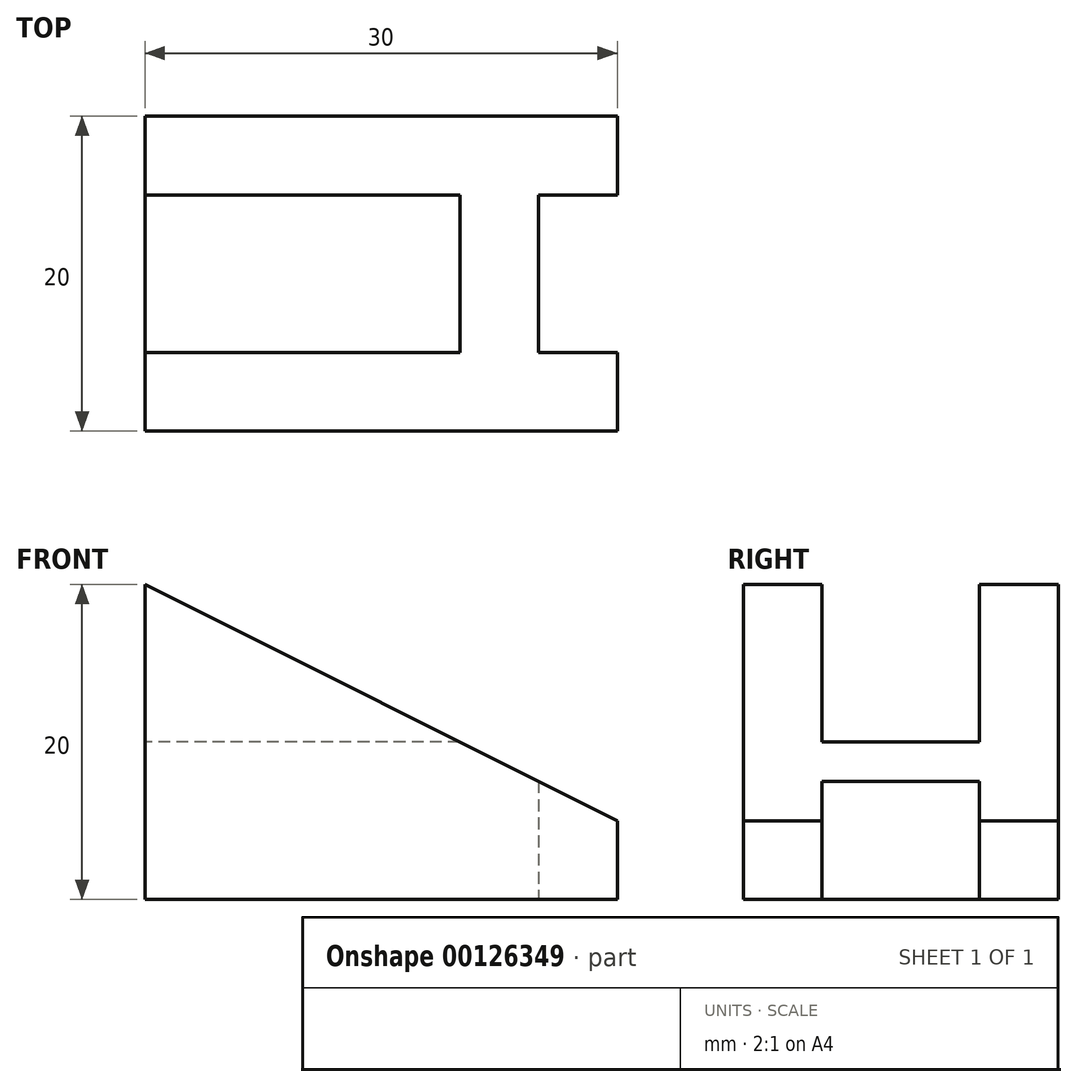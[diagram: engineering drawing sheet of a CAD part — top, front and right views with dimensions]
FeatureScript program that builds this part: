
annotation { "Feature Type Name" : "Feature", "Feature Type Description" : "" }
export const myFeature = defineFeature(function(context is Context, id is Id, definition is map)
    precondition{}
    {
        {
            var Q0;
            Q0=qCreatedBy(makeId("Front.planeOp"),FACE);
            var sketch = newSketch(context, id + "F0", { "sketchPlane" : qUnion([Q0])});
            skLineSegment(sketch, "E0", {"start": v(0, 0) * mm, "end": v(0, 20) * mm});
            skLineSegment(sketch, "E1", {"start": v(0, 20) * mm, "end": v(30, 5) * mm});
            skLineSegment(sketch, "E2", {"start": v(30, 5) * mm, "end": v(30, 0) * mm});
            skLineSegment(sketch, "E3", {"start": v(30, 0) * mm, "end": v(0, 0) * mm});
            skSolve(sketch);
        }
        {
            var Q0;
            Q0 = qSketchRegion(id + "F0", true);
            extrude(context, id + "F1", {"entities" : qUnion([Q0]), "endBound" : BoundingType.SYMMETRIC, "depth" : 20 * mm});
        }
        {
            var Q0;
            Q0=makeQuery(id+"F1.opExtrude","SWEPT_FACE",FACE,{"disambiguationData":[OSD([sQuery(id+"F0.wireOp",EDGE,"E3")])]});
            var sketch = newSketch(context, id + "F2", { "sketchPlane" : qUnion([Q0])});
            skLineSegment(sketch, "E4", {"start": v(30, -5) * mm, "end": v(25, -5) * mm});
            skLineSegment(sketch, "E5", {"start": v(25, -5) * mm, "end": v(25, 5) * mm});
            skLineSegment(sketch, "E6", {"start": v(25, 5) * mm, "end": v(30, 5) * mm});
            skLineSegment(sketch, "E7", {"start": v(30, 5) * mm, "end": v(30, -5) * mm});
            skSolve(sketch);
        }
        {
            var Q0;
            Q0 = qSketchRegion(id + "F2", true);
            extrude(context, id + "F3", {"entities" : qUnion([Q0]), "operationType" : NewBodyOperationType.REMOVE, "oppositeDirection" : true, "depth" : 25 * mm});
        }
        {
            var Q0;
            Q0=makeQuery(id+"F1.opExtrude","SWEPT_FACE",FACE,{"disambiguationData":[OSD([sQuery(id+"F0.wireOp",EDGE,"E0")])]});
            var sketch = newSketch(context, id + "F4", { "sketchPlane" : qUnion([Q0])});
            skLineSegment(sketch, "E8", {"start": v(-5, 20) * mm, "end": v(-5, 10) * mm});
            skLineSegment(sketch, "E9", {"start": v(-5, 10) * mm, "end": v(5, 10) * mm});
            skLineSegment(sketch, "E10", {"start": v(5, 10) * mm, "end": v(5, 20) * mm});
            skLineSegment(sketch, "E11", {"start": v(5, 20) * mm, "end": v(-5, 20) * mm});
            skSolve(sketch);
        }
        {
            var Q0;
            Q0 = qSketchRegion(id + "F4", true);
            extrude(context, id + "F5", {"entities" : qUnion([Q0]), "operationType" : NewBodyOperationType.REMOVE, "oppositeDirection" : true, "depth" : 25 * mm});
        }
    });
